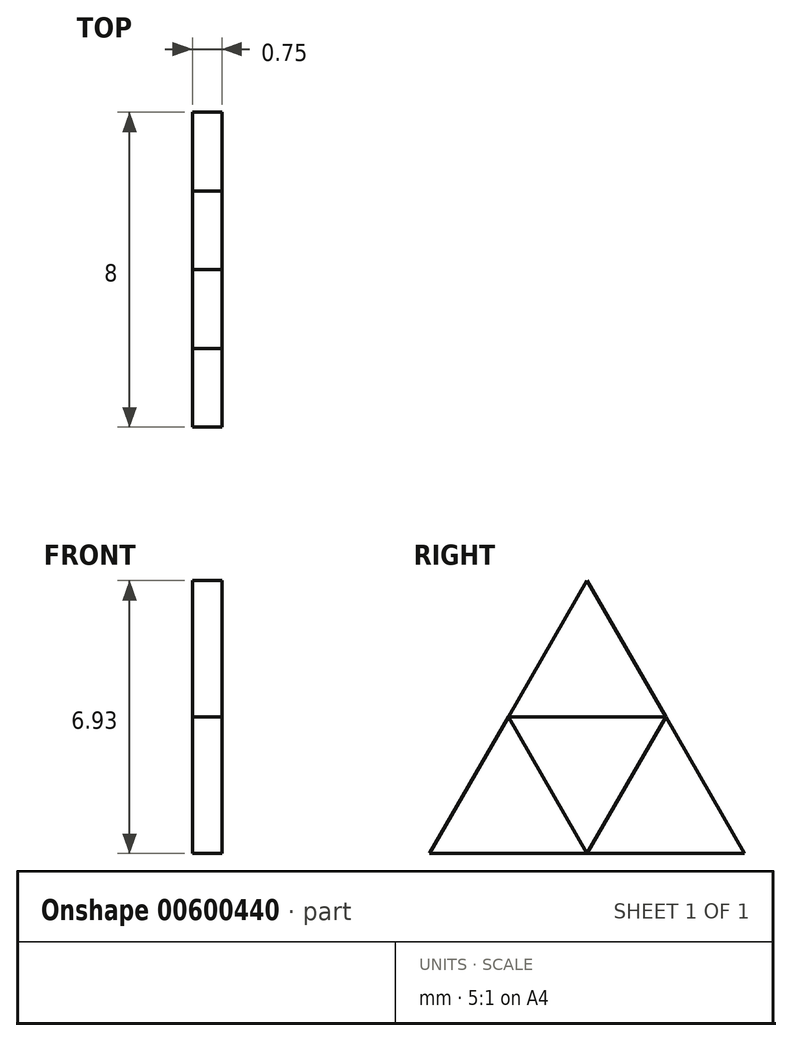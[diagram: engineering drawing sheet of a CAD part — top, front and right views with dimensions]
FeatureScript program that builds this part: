
annotation { "Feature Type Name" : "Feature", "Feature Type Description" : "" }
export const myFeature = defineFeature(function(context is Context, id is Id, definition is map)
    precondition{}
    {
        {
            var Q0;
            Q0=qCreatedBy(makeId("Right.planeOp"),FACE);
            var sketch = newSketch(context, id + "F0", { "sketchPlane" : qUnion([Q0])});
            skLineSegment(sketch, "E0", {"start": v(-6, 3.46) * mm, "end": v(-4, 6.93) * mm});
            skLineSegment(sketch, "E1", {"start": v(-4, 6.93) * mm, "end": v(-2, 3.46) * mm});
            skLineSegment(sketch, "E2", {"start": v(-2, 3.46) * mm, "end": v(-6, 3.46) * mm});
            skLineSegment(sketch, "E3", {"start": v(-8, 0) * mm, "end": v(-6, 3.46) * mm});
            skLineSegment(sketch, "E4", {"start": v(-6, 3.46) * mm, "end": v(-4, 0) * mm});
            skLineSegment(sketch, "E5", {"start": v(-4, 0) * mm, "end": v(-8, 0) * mm});
            skLineSegment(sketch, "E6", {"start": v(0, 0) * mm, "end": v(-2, 3.46) * mm});
            skLineSegment(sketch, "E7", {"start": v(-2, 3.46) * mm, "end": v(-4, 0) * mm});
            skLineSegment(sketch, "E8", {"start": v(0, 0) * mm, "end": v(-4, 0) * mm});
            skSolve(sketch);
        }
        {
            var Q0;
            Q0 = qSketchRegion(id + "F0", true);
            extrude(context, id + "F1", {"entities" : qUnion([Q0]), "depth" : .75 * mm, "offsetDistance" : 25 * mm});
        }
        {
            var Q0;
            Q0=makeQuery(id+"F1.opExtrude","CAP_FACE",FACE,{"disambiguationData":[OSD([sQuery(id+"F0.wireOp",EDGE,"E0"),sQuery(id+"F0.wireOp",EDGE,"E1"),sQuery(id+"F0.wireOp",EDGE,"E3"),sQuery(id+"F0.wireOp",EDGE,"E5"),sQuery(id+"F0.wireOp",EDGE,"E6"),sQuery(id+"F0.wireOp",EDGE,"E8")])],"isStart":false});
            var sketch = newSketch(context, id + "F2", { "sketchPlane" : qUnion([Q0])});
            skLineSegment(sketch, "E9", {"start": v(-4, 0) * mm, "end": v(-6, 3.46) * mm});
            skLineSegment(sketch, "E10", {"start": v(-6, 3.46) * mm, "end": v(-2, 3.46) * mm});
            skLineSegment(sketch, "E11", {"start": v(-2, 3.46) * mm, "end": v(-4, 0) * mm});
            skSolve(sketch);
        }
        {
            var Q0;
            Q0 = qSketchRegion(id + "F2", true);
            extrude(context, id + "F3", {"entities" : qUnion([Q0]), "operationType" : NewBodyOperationType.REMOVE, "endBound" : BoundingType.UP_TO_NEXT, "oppositeDirection" : true, "depth" : 25 * mm, "offsetDistance" : 25 * mm});
        }
    });
